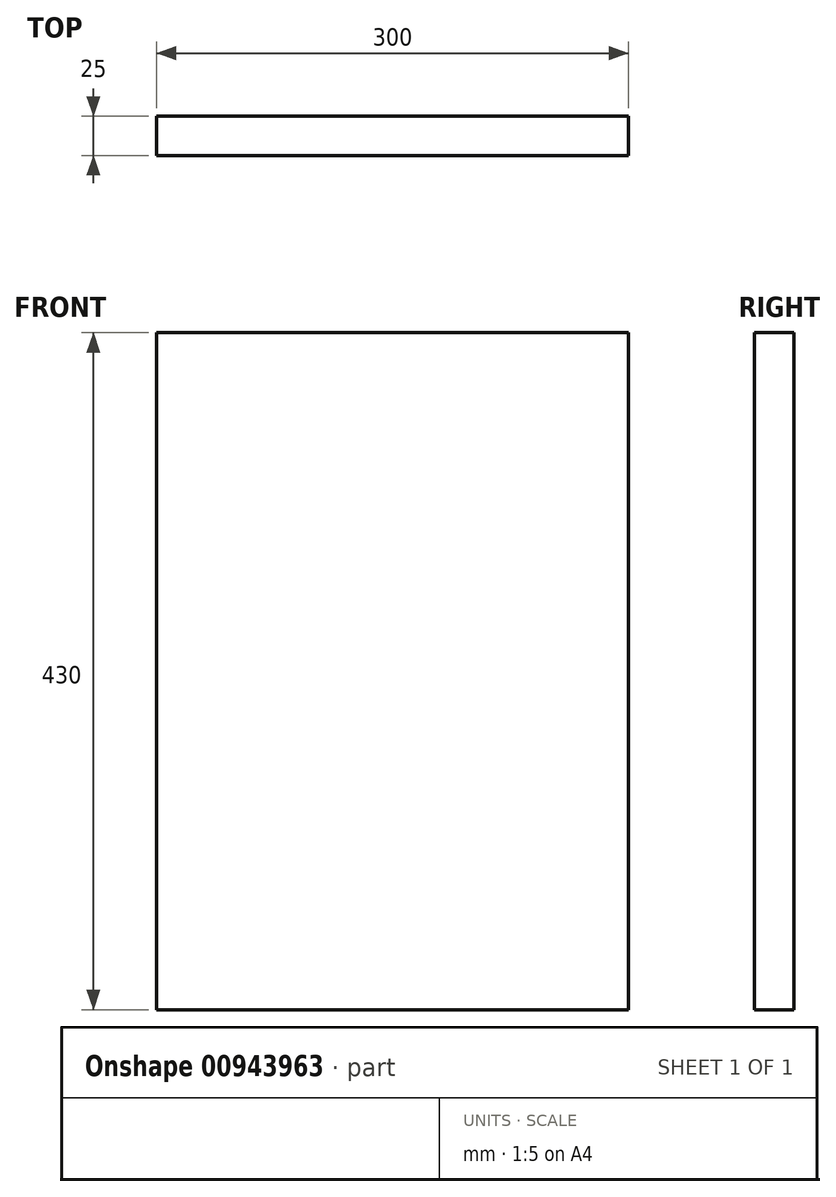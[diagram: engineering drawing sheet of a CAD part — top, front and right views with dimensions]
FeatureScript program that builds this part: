
annotation { "Feature Type Name" : "Feature", "Feature Type Description" : "" }
export const myFeature = defineFeature(function(context is Context, id is Id, definition is map)
    precondition{}
    {
        {
            var Q0;
            Q0=qCreatedBy(makeId("Front.planeOp"),FACE);
            var sketch = newSketch(context, id + "F0", { "sketchPlane" : qUnion([Q0])});
            skLineSegment(sketch, "E0.bottom", {"start": v(150, -215) * mm, "end": v(-150, -215) * mm});
            skLineSegment(sketch, "E0.top", {"start": v(150, 215) * mm, "end": v(-150, 215) * mm});
            skLineSegment(sketch, "E0.left", {"start": v(150, -215) * mm, "end": v(150, 215) * mm});
            skLineSegment(sketch, "E0.right", {"start": v(-150, -215) * mm, "end": v(-150, 215) * mm});
            skPoint(sketch, "E0.middle", {"position": v(0, 0) * mm});
            skSolve(sketch);
        }
        {
            var Q0;
            Q0=makeQuery(id+"F0.imprint","IMPRINT",FACE,{"disambiguationData":[TD([[makeQuery(id+"F0.imprint","IMPRINT",EDGE,{"derivedFrom":sQuery(id+"F0.wireOp",EDGE,"E0.bottom")}),-1.0]])]});
            extrude(context, id + "F1", {"entities" : qUnion([Q0]), "depth" : 25 * mm, "offsetDistance" : 25 * mm});
        }
    });
